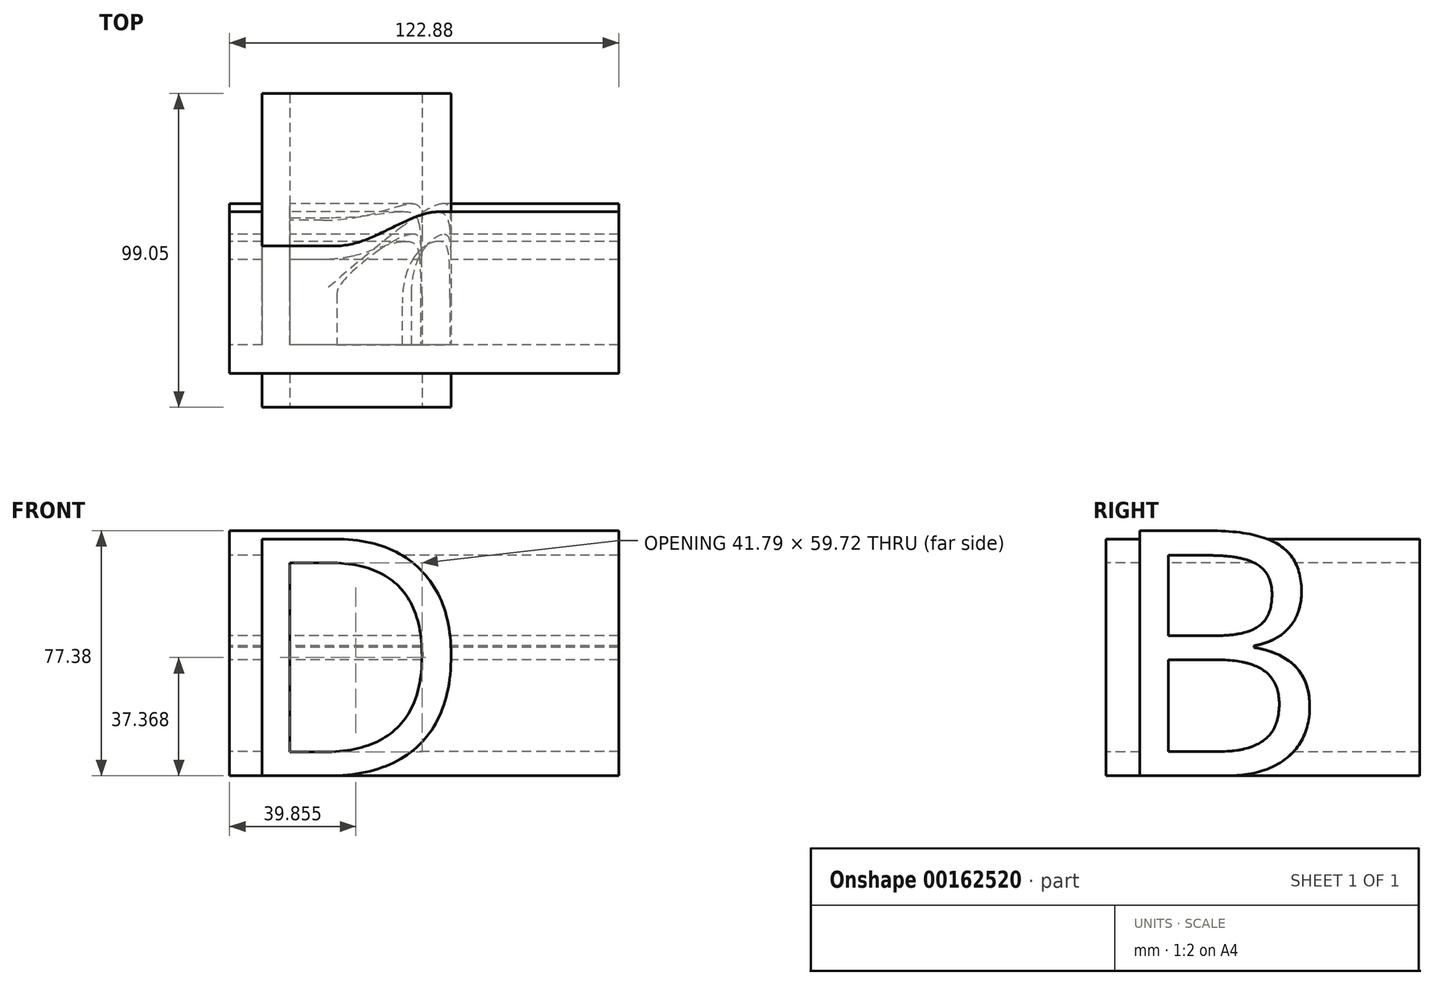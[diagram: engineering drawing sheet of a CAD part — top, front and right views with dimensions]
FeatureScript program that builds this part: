
annotation { "Feature Type Name" : "Feature", "Feature Type Description" : "" }
export const myFeature = defineFeature(function(context is Context, id is Id, definition is map)
    precondition{}
    {
        {
            var Q0;
            Q0=qCreatedBy(makeId("Front.planeOp"),FACE);
            var sketch = newSketch(context, id + "F0", { "sketchPlane" : qUnion([Q0])});
            skText(sketch, "E0", { "text": "D", "fontName": "OpenSans-Regular.ttf"});
            const initialGuessF0  = {"E0": [0, 0, 1, 0, 0.07539]};
            skSetInitialGuess(sketch, initialGuessF0);
            skSolve(sketch);
        }
        {
            var Q0;
            Q0=qCreatedBy(makeId("Right.planeOp"),FACE);
            var sketch = newSketch(context, id + "F1", { "sketchPlane" : qUnion([Q0])});
            skText(sketch, "E1", { "text": "B", "fontName": "OpenSans-Regular.ttf"});
            const initialGuessF1  = {"E1": [0, 0, 1, 0, 0.07804]};
            skSetInitialGuess(sketch, initialGuessF1);
            skSolve(sketch);
        }
        {
            var Q0;
            Q0=makeQuery(id+"F0.imprint","IMPRINT",FACE,{"disambiguationData":[TD([[makeQuery(id+"F0.imprint","IMPRINT",EDGE,{"derivedFrom":sQuery(id+"F0.wireOp",EDGE,"E0.sketch_text.stroke-0")}),-1.0]])]});
            extrude(context, id + "F2", {"entities" : qUnion([Q0]), "oppositeDirection" : true, "depth" : 99.05 * mm});
        }
        {
            var Q0;
            Q0=makeQuery(id+"F1.imprint","IMPRINT",FACE,{"disambiguationData":[TD([[makeQuery(id+"F1.imprint","IMPRINT",EDGE,{"derivedFrom":sQuery(id+"F1.wireOp",EDGE,"E1.sketch_text.stroke-0")}),-1.0]])]});
            extrude(context, id + "F3", {"entities" : qUnion([Q0]), "operationType" : NewBodyOperationType.ADD, "depth" : 122.88 * mm});
        }
    });
